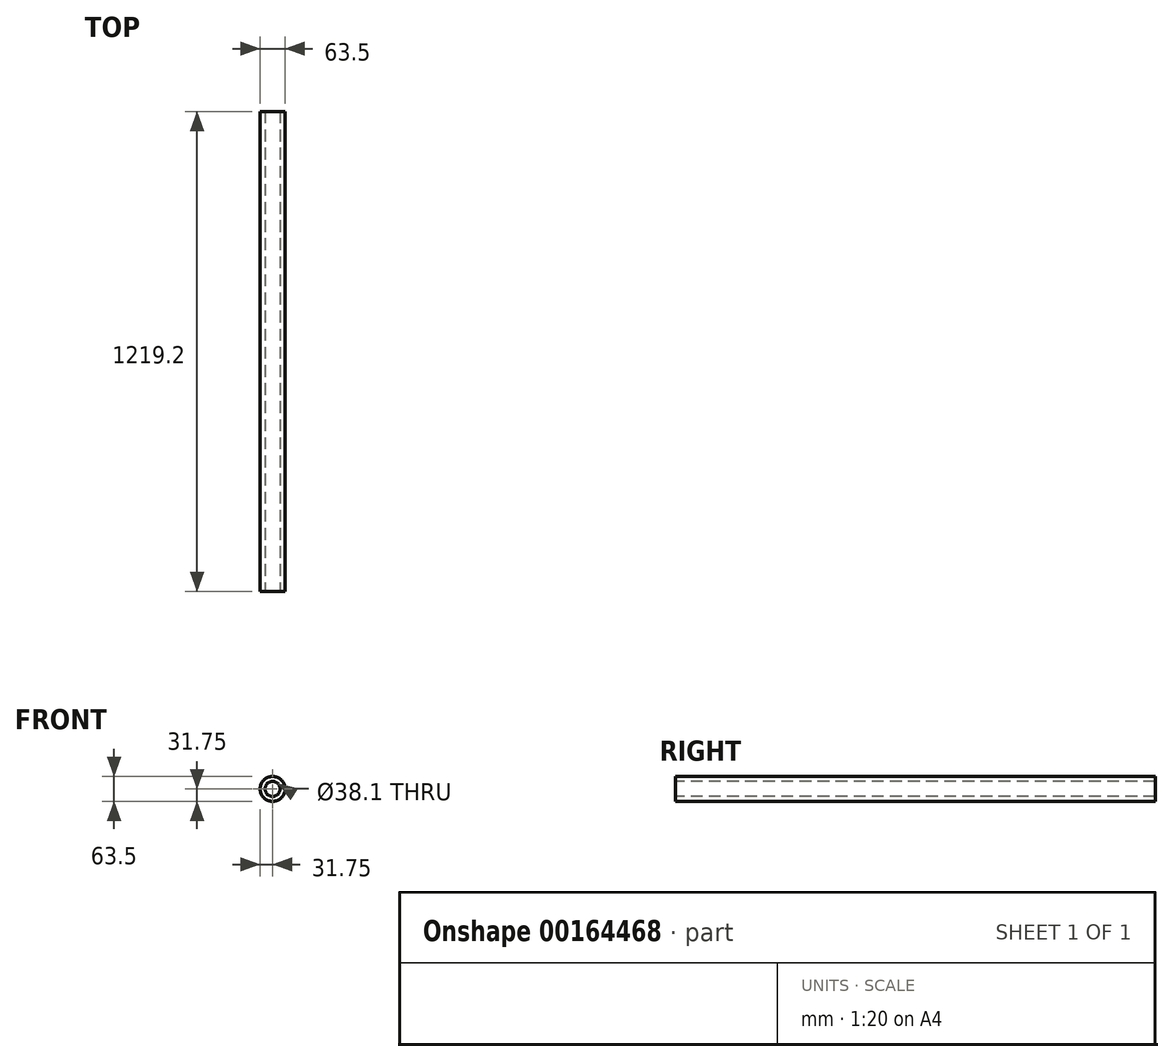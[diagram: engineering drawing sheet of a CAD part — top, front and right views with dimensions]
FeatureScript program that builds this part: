
annotation { "Feature Type Name" : "Feature", "Feature Type Description" : "" }
export const myFeature = defineFeature(function(context is Context, id is Id, definition is map)
    precondition{}
    {
        {
            var Q0;
            Q0=qCreatedBy(makeId("Front.planeOp"),FACE);
            var sketch = newSketch(context, id + "F0", { "sketchPlane" : qUnion([Q0])});
            skCircle(sketch, "E0", {"center": v(0, 0) * mm, "radius": 31.75 * mm});
            skCircle(sketch, "E1", {"center": v(0, 0) * mm, "radius": 19.05 * mm});
            skSolve(sketch);
        }
        {
            var Q0;
            Q0=makeQuery(id+"F0.imprint","IMPRINT",FACE,{"disambiguationData":[TD([[makeQuery(id+"F0.imprint","IMPRINT",EDGE,{"derivedFrom":sQuery(id+"F0.wireOp",EDGE,"E0")}),1.0]])]});
            extrude(context, id + "F1", {"entities" : qUnion([Q0]), "oppositeDirection" : true, "depth" : 1219.2 * mm});
        }
    });
